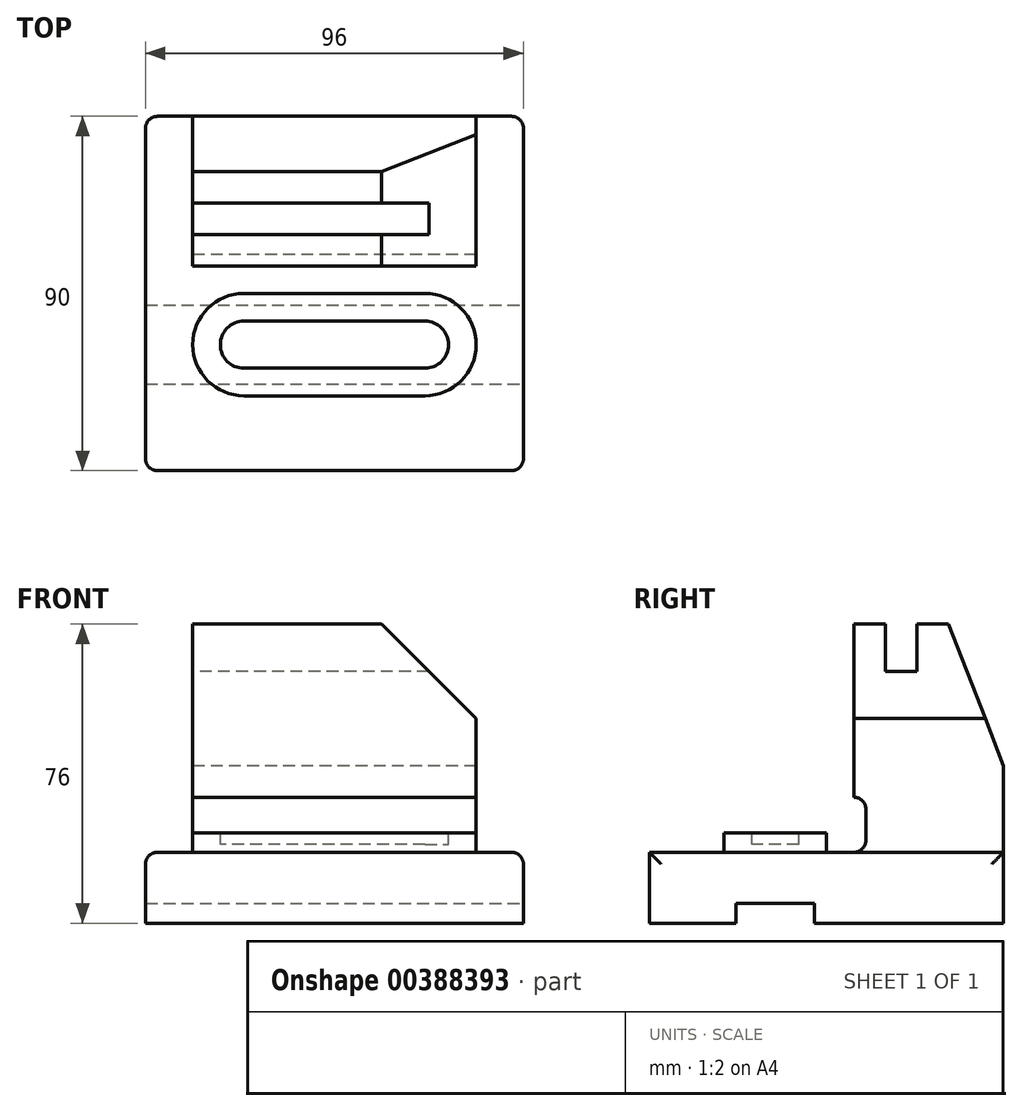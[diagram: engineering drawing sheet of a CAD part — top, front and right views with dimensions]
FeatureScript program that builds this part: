
annotation { "Feature Type Name" : "Feature", "Feature Type Description" : "" }
export const myFeature = defineFeature(function(context is Context, id is Id, definition is map)
    precondition{}
    {
        {
            var Q0;
            Q0=qCreatedBy(makeId("Top.planeOp"),FACE);
            var sketch = newSketch(context, id + "F0", { "sketchPlane" : qUnion([Q0])});
            skLineSegment(sketch, "E0.bottom", {"start": v(0, 0) * mm, "end": v(96, 0) * mm});
            skLineSegment(sketch, "E0.top", {"start": v(0, 90) * mm, "end": v(96, 90) * mm});
            skLineSegment(sketch, "E0.left", {"start": v(0, 0) * mm, "end": v(0, 90) * mm});
            skLineSegment(sketch, "E0.right", {"start": v(96, 0) * mm, "end": v(96, 90) * mm});
            skSolve(sketch);
        }
        {
            var Q0;
            Q0 = qSketchRegion(id + "F0", true);
            extrude(context, id + "F1", {"entities" : qUnion([Q0]), "depth" : 18 * mm});
        }
        {
            var Q0;
            Q0=makeQuery(id+"F1.opExtrude","CAP_FACE",FACE,{"disambiguationData":[OSD([sQuery(id+"F0.wireOp",EDGE,"E0.bottom"),sQuery(id+"F0.wireOp",EDGE,"E0.top"),sQuery(id+"F0.wireOp",EDGE,"E0.left"),sQuery(id+"F0.wireOp",EDGE,"E0.right")])],"isStart":false});
            var sketch = newSketch(context, id + "F2", { "sketchPlane" : qUnion([Q0])});
            skLineSegment(sketch, "E1.bottom", {"start": v(12, 90) * mm, "end": v(84, 90) * mm});
            skLineSegment(sketch, "E1.top", {"start": v(12, 52) * mm, "end": v(84, 52) * mm});
            skLineSegment(sketch, "E1.left", {"start": v(12, 90) * mm, "end": v(12, 52) * mm});
            skLineSegment(sketch, "E1.right", {"start": v(84, 90) * mm, "end": v(84, 52) * mm});
            skSolve(sketch);
        }
        {
            var Q0;
            Q0=makeQuery(id+"F1.opExtrude","CAP_FACE",FACE,{"disambiguationData":[OSD([sQuery(id+"F0.wireOp",EDGE,"E0.bottom"),sQuery(id+"F0.wireOp",EDGE,"E0.top"),sQuery(id+"F0.wireOp",EDGE,"E0.left"),sQuery(id+"F0.wireOp",EDGE,"E0.right")])],"isStart":true});
            cPlane(context, id + "F3", {"entities" : qUnion([Q0]), "cplaneType" : CPlaneType.OFFSET, "offset" : 76 * mm, "oppositeDirection" : true, "width" : 150 * mm, "height" : 150 * mm});
        }
        {
            var Q0;
            Q0=makeQuery(id+"F2.imprint","IMPRINT",FACE,{"disambiguationData":[TD([[makeQuery(id+"F2.imprint","IMPRINT",EDGE,{"derivedFrom":sQuery(id+"F2.wireOp",EDGE,"E1.bottom")}),-1.0]])]});
            var Q1;
            Q1=qCreatedBy(id+"F3.planeOp",FACE);
            extrude(context, id + "F4", {"entities" : qUnion([Q0]), "operationType" : NewBodyOperationType.ADD, "endBound" : BoundingType.UP_TO_SURFACE, "endBoundEntityFace" : qUnion([Q1]), "depth" : 0.6 * mm});
        }
        {
            var Q0;
            Q0=makeQuery(id+"F4.opExtrude","SWEPT_FACE",FACE,{"disambiguationData":[OSD([sQuery(id+"F2.wireOp",EDGE,"E1.top")])]});
            var sketch = newSketch(context, id + "F5", { "sketchPlane" : qUnion([Q0])});
            skLineSegment(sketch, "E2", {"start": v(84, 76) * mm, "end": v(60, 76) * mm});
            skLineSegment(sketch, "E3", {"start": v(60, 76) * mm, "end": v(84, 52) * mm});
            skLineSegment(sketch, "E4", {"start": v(84, 52) * mm, "end": v(84, 76) * mm});
            skSolve(sketch);
        }
        {
            var Q0;
            Q0 = qSketchRegion(id + "F5", true);
            var Q1;
            Q1=makeQuery(id+"F4.boolean.opBoolean","MERGE",FACE,{"derivedFrom":[makeQuery(id+"F1.opExtrude","SWEPT_FACE",FACE,{"disambiguationData":[OSD([sQuery(id+"F0.wireOp",EDGE,"E0.top")])]}),makeQuery(id+"F4.opExtrude","SWEPT_FACE",FACE,{"disambiguationData":[OSD([sQuery(id+"F2.wireOp",EDGE,"E1.bottom")])]})]});
            extrude(context, id + "F6", {"entities" : qUnion([Q0]), "operationType" : NewBodyOperationType.REMOVE, "endBound" : BoundingType.UP_TO_SURFACE, "oppositeDirection" : true, "endBoundEntityFace" : qUnion([Q1]), "depth" : 25 * mm});
        }
        {
            var Q0;
            Q0=makeQuery(id+"F4.opExtrude","SWEPT_FACE",FACE,{"disambiguationData":[OSD([sQuery(id+"F2.wireOp",EDGE,"E1.left")])]});
            var sketch = newSketch(context, id + "F7", { "sketchPlane" : qUnion([Q0])});
            skLineSegment(sketch, "E5.bottom", {"start": v(-60, 76) * mm, "end": v(-68, 76) * mm});
            skLineSegment(sketch, "E5.top", {"start": v(-60, 64) * mm, "end": v(-68, 64) * mm});
            skLineSegment(sketch, "E5.left", {"start": v(-60, 76) * mm, "end": v(-60, 64) * mm});
            skLineSegment(sketch, "E5.right", {"start": v(-68, 76) * mm, "end": v(-68, 64) * mm});
            skSolve(sketch);
        }
        {
            var Q0;
            Q0 = qSketchRegion(id + "F7", true);
            extrude(context, id + "F8", {"entities" : qUnion([Q0]), "operationType" : NewBodyOperationType.REMOVE, "endBound" : BoundingType.UP_TO_NEXT, "oppositeDirection" : true, "depth" : 25 * mm});
        }
        {
            var Q0;
            Q0=makeQuery(id+"F4.opExtrude","SWEPT_FACE",FACE,{"disambiguationData":[OSD([sQuery(id+"F2.wireOp",EDGE,"E1.left")])]});
            var sketch = newSketch(context, id + "F9", { "sketchPlane" : qUnion([Q0])});
            skLineSegment(sketch, "E6", {"start": v(-76, 76) * mm, "end": v(-90, 40) * mm});
            skLineSegment(sketch, "E7", {"start": v(-90, 40) * mm, "end": v(-90, 76) * mm});
            skLineSegment(sketch, "E8", {"start": v(-90, 76) * mm, "end": v(-76, 76) * mm});
            skSolve(sketch);
        }
        {
            var Q0;
            Q0=makeQuery(id+"F9.imprint","IMPRINT",FACE,{"disambiguationData":[TD([[makeQuery(id+"F9.imprint","IMPRINT",EDGE,{"derivedFrom":sQuery(id+"F9.wireOp",EDGE,"E6")}),-1.0]])]});
            extrude(context, id + "F10", {"entities" : qUnion([Q0]), "operationType" : NewBodyOperationType.REMOVE, "endBound" : BoundingType.UP_TO_NEXT, "oppositeDirection" : true, "depth" : 36.7 * mm});
        }
        {
            var Q0;
            Q0=makeQuery(id+"F1.opExtrude","SWEPT_FACE",FACE,{"disambiguationData":[OSD([sQuery(id+"F0.wireOp",EDGE,"E0.right")])]});
            var sketch = newSketch(context, id + "F11", { "sketchPlane" : qUnion([Q0])});
            skLineSegment(sketch, "E9.bottom", {"start": v(22, 0) * mm, "end": v(42, 0) * mm});
            skLineSegment(sketch, "E9.top", {"start": v(22, 5) * mm, "end": v(42, 5) * mm});
            skLineSegment(sketch, "E9.left", {"start": v(22, 0) * mm, "end": v(22, 5) * mm});
            skLineSegment(sketch, "E9.right", {"start": v(42, 0) * mm, "end": v(42, 5) * mm});
            skPoint(sketch, "E10", {"position": v(32, 5) * mm});
            skSolve(sketch);
        }
        {
            var Q0;
            Q0 = qSketchRegion(id + "F11", true);
            extrude(context, id + "F12", {"entities" : qUnion([Q0]), "operationType" : NewBodyOperationType.REMOVE, "endBound" : BoundingType.UP_TO_NEXT, "oppositeDirection" : true, "depth" : 24.5 * mm});
        }
        {
            var Q0;
            Q0=makeQuery(id+"F1.opExtrude","CAP_FACE",FACE,{"disambiguationData":[OSD([sQuery(id+"F0.wireOp",EDGE,"E0.bottom"),sQuery(id+"F0.wireOp",EDGE,"E0.top"),sQuery(id+"F0.wireOp",EDGE,"E0.left"),sQuery(id+"F0.wireOp",EDGE,"E0.right")])],"isStart":false});
            var sketch = newSketch(context, id + "F13", { "sketchPlane" : qUnion([Q0])});
            skLineSegment(sketch, "E11.bottom", {"start": v(25, 45) * mm, "end": v(71, 45) * mm});
            skLineSegment(sketch, "E11.top", {"start": v(25, 19) * mm, "end": v(71, 19) * mm});
            skLineSegment(sketch, "E11.left", {"start": v(25, 45) * mm, "end": v(25, 19) * mm});
            skLineSegment(sketch, "E11.right", {"start": v(71, 45) * mm, "end": v(71, 19) * mm});
            skLineSegment(sketch, "E12", {"start": v(25, 32) * mm, "end": v(71, 32) * mm, "construction": true});
            skArc(sketch, "E13", {"start": v(25, 45) * mm, "mid": v(12, 32) * mm, "end": v(25, 19) * mm});
            skArc(sketch, "E14", {"start": v(71, 19) * mm, "mid": v(84, 32) * mm, "end": v(71, 45) * mm});
            skSolve(sketch);
        }
        {
            var Q0;
            Q0=makeQuery(id+"F13.imprint","IMPRINT",FACE,{"disambiguationData":[TD([[makeQuery(id+"F13.imprint","IMPRINT",EDGE,{"derivedFrom":sQuery(id+"F13.wireOp",EDGE,"E11.bottom")}),-1.0]])]});
            var Q1;
            Q1=makeQuery(id+"F13.imprint","IMPRINT",FACE,{"disambiguationData":[TD([[makeQuery(id+"F13.imprint","IMPRINT",EDGE,{"derivedFrom":sQuery(id+"F13.wireOp",EDGE,"E11.left")}),-1.0]])]});
            var Q2;
            Q2=makeQuery(id+"F13.imprint","IMPRINT",FACE,{"disambiguationData":[TD([[makeQuery(id+"F13.imprint","IMPRINT",EDGE,{"derivedFrom":sQuery(id+"F13.wireOp",EDGE,"E11.right")}),1.0]])]});
            extrude(context, id + "F14", {"entities" : qUnion([Q0, Q1, Q2]), "operationType" : NewBodyOperationType.ADD, "depth" : 5 * mm});
        }
        {
            var Q0;
            Q0=makeQuery(id+"F14.opExtrude","CAP_FACE",FACE,{"disambiguationData":[OSD([sQuery(id+"F13.wireOp",EDGE,"E11.bottom"),sQuery(id+"F13.wireOp",EDGE,"E11.top"),sQuery(id+"F13.wireOp",EDGE,"E13"),sQuery(id+"F13.wireOp",EDGE,"E14")])],"isStart":false});
            var sketch = newSketch(context, id + "F15", { "sketchPlane" : qUnion([Q0])});
            skLineSegment(sketch, "E15.bottom", {"start": v(25, 38) * mm, "end": v(71, 38) * mm});
            skLineSegment(sketch, "E15.top", {"start": v(25, 26) * mm, "end": v(71, 26) * mm});
            skLineSegment(sketch, "E15.left", {"start": v(25, 38) * mm, "end": v(25, 26) * mm});
            skLineSegment(sketch, "E15.right", {"start": v(71, 38) * mm, "end": v(71, 26) * mm});
            skLineSegment(sketch, "E16", {"start": v(25, 32) * mm, "end": v(71, 32) * mm, "construction": true});
            skArc(sketch, "E17", {"start": v(25, 38) * mm, "mid": v(19, 32) * mm, "end": v(25, 26) * mm});
            skArc(sketch, "E18", {"start": v(71, 26) * mm, "mid": v(77, 32) * mm, "end": v(71, 38) * mm});
            skSolve(sketch);
        }
        {
            var Q0;
            Q0=makeQuery(id+"F0.imprint","IMPRINT",FACE,{"disambiguationData":[TD([[makeQuery(id+"F0.imprint","IMPRINT",EDGE,{"derivedFrom":sQuery(id+"F0.wireOp",EDGE,"E0.bottom")}),1.0]])]});
            cPlane(context, id + "F16", {"entities" : qUnion([Q0]), "cplaneType" : CPlaneType.OFFSET, "offset" : 20 * mm, "width" : 150 * mm, "height" : 150 * mm});
        }
        {
            var Q0;
            Q0 = qSketchRegion(id + "F15", true);
            var Q1;
            Q1=qCreatedBy(id+"F16.planeOp",FACE);
            extrude(context, id + "F17", {"entities" : qUnion([Q0]), "operationType" : NewBodyOperationType.REMOVE, "endBound" : BoundingType.UP_TO_SURFACE, "oppositeDirection" : true, "endBoundEntityFace" : qUnion([Q1]), "depth" : 3 * mm});
        }
        {
            var Q0;
            Q0=makeQuery(id+"F4.opExtrude","SWEPT_FACE",FACE,{"disambiguationData":[OSD([sQuery(id+"F2.wireOp",EDGE,"E1.right")])]});
            var sketch = newSketch(context, id + "F18", { "sketchPlane" : qUnion([Q0])});
            skLineSegment(sketch, "E19.bottom", {"start": v(52, 18) * mm, "end": v(55, 18) * mm});
            skLineSegment(sketch, "E19.top", {"start": v(52, 32) * mm, "end": v(55, 32) * mm});
            skLineSegment(sketch, "E19.left", {"start": v(52, 18) * mm, "end": v(52, 32) * mm});
            skLineSegment(sketch, "E19.right", {"start": v(55, 18) * mm, "end": v(55, 32) * mm});
            skSolve(sketch);
        }
        {
            var Q0;
            Q0 = qSketchRegion(id + "F18", true);
            extrude(context, id + "F19", {"entities" : qUnion([Q0]), "operationType" : NewBodyOperationType.REMOVE, "endBound" : BoundingType.UP_TO_NEXT, "oppositeDirection" : true, "depth" : 25 * mm});
        }
        {
            var Q0;
            Q0=makeQuery(id+"F14.opExtrude","CAP_EDGE",EDGE,{"disambiguationData":[OSD([sQuery(id+"F13.wireOp",EDGE,"E11.top")])],"isStart":true});
            var Q1;
            Q1=makeQuery(id+"F19.boolean.opBoolean","COPY",EDGE,{"derivedFrom":makeQuery(id+"F19.opExtrude","SWEPT_EDGE",EDGE,{"disambiguationData":[OSD([sQuery(id+"F2.wireOp",EDGE,"E1.right"),sQuery(id+"F18.wireOp",EDGE,"E19.bottom"),sQuery(id+"F18.wireOp",EDGE,"E19.right")])]})});
            var Q2;
            Q2=makeQuery(id+"F19.boolean.opBoolean","COPY",EDGE,{"derivedFrom":makeQuery(id+"F19.opExtrude","SWEPT_EDGE",EDGE,{"disambiguationData":[OSD([sQuery(id+"F18.wireOp",EDGE,"E19.top"),sQuery(id+"F18.wireOp",EDGE,"E19.right")])]})});
            var Q3;
            Q3=makeQuery(id+"F4.opExtrude","CAP_EDGE",EDGE,{"disambiguationData":[OSD([sQuery(id+"F2.wireOp",EDGE,"E1.right")])],"isStart":true});
            var Q4;
            Q4=makeQuery(id+"F4.opExtrude","CAP_EDGE",EDGE,{"disambiguationData":[OSD([sQuery(id+"F2.wireOp",EDGE,"E1.left")])],"isStart":true});
            var Q5;
            Q5=makeQuery(id+"F1.opExtrude","CAP_EDGE",EDGE,{"disambiguationData":[OSD([sQuery(id+"F0.wireOp",EDGE,"E0.left")])],"isStart":false});
            var Q6;
            Q6=makeQuery(id+"F1.opExtrude","CAP_EDGE",EDGE,{"disambiguationData":[OSD([sQuery(id+"F0.wireOp",EDGE,"E0.right")])],"isStart":false});
            var Q7;
            Q7=makeQuery(id+"F1.opExtrude","SWEPT_EDGE",EDGE,{"disambiguationData":[OSD([sQuery(id+"F0.wireOp",EDGE,"E0.bottom"),sQuery(id+"F0.wireOp",EDGE,"E0.right")])]});
            var Q8;
            Q8=makeQuery(id+"F1.opExtrude","SWEPT_EDGE",EDGE,{"disambiguationData":[OSD([sQuery(id+"F0.wireOp",EDGE,"E0.bottom"),sQuery(id+"F0.wireOp",EDGE,"E0.left")])]});
            var Q9;
            Q9=makeQuery(id+"F1.opExtrude","SWEPT_EDGE",EDGE,{"disambiguationData":[OSD([sQuery(id+"F0.wireOp",EDGE,"E0.top"),sQuery(id+"F0.wireOp",EDGE,"E0.left")])]});
            var Q10;
            Q10=makeQuery(id+"F1.opExtrude","SWEPT_EDGE",EDGE,{"disambiguationData":[OSD([sQuery(id+"F0.wireOp",EDGE,"E0.top"),sQuery(id+"F0.wireOp",EDGE,"E0.right")])]});
            fillet(context, id + "F20", {"entities" : qUnion([Q0, Q1, Q2, Q3, Q4, Q5, Q6, Q7, Q8, Q9, Q10]), "radius" : 3 * mm, "tangentPropagation" : true, "allowEdgeOverflow" : false});
        }
    });
